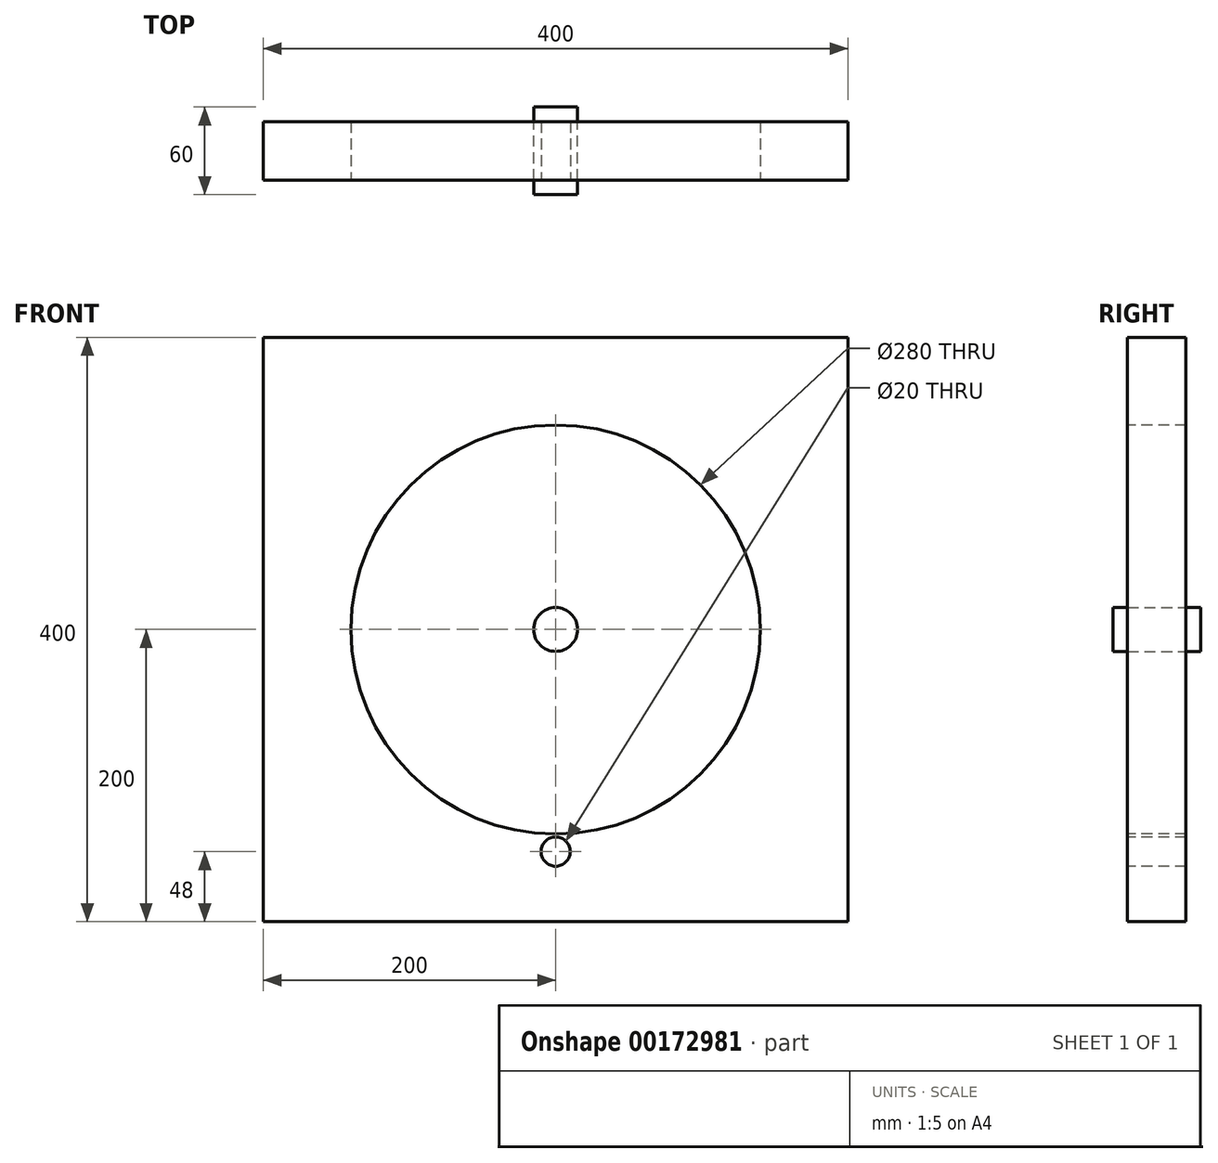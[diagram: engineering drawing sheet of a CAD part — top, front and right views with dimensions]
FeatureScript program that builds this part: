
annotation { "Feature Type Name" : "Feature", "Feature Type Description" : "" }
export const myFeature = defineFeature(function(context is Context, id is Id, definition is map)
    precondition{}
    {
        {
            var Q0;
            Q0=qCreatedBy(makeId("Top.planeOp"),FACE);
            var sketch = newSketch(context, id + "F0", { "sketchPlane" : qUnion([Q0])});
            skLineSegment(sketch, "E0.bottom", {"start": v(200, -20) * mm, "end": v(-200, -20) * mm});
            skLineSegment(sketch, "E0.top", {"start": v(200, 20) * mm, "end": v(-200, 20) * mm});
            skLineSegment(sketch, "E0.left", {"start": v(200, -20) * mm, "end": v(200, 20) * mm});
            skLineSegment(sketch, "E0.right", {"start": v(-200, -20) * mm, "end": v(-200, 20) * mm});
            skPoint(sketch, "E0.middle", {"position": v(0, 0) * mm});
            skSolve(sketch);
        }
        {
            var Q0;
            Q0 = qSketchRegion(id + "F0", true);
            extrude(context, id + "F1", {"entities" : qUnion([Q0]), "depth" : 200 * mm, "hasSecondDirection" : true, "secondDirectionOppositeDirection" : true, "secondDirectionDepth" : 200 * mm});
        }
        {
            var Q0;
            Q0=makeQuery(id+"F1.opExtrude","SWEPT_FACE",FACE,{"disambiguationData":[OSD([sQuery(id+"F0.wireOp",EDGE,"E0.bottom")])]});
            var sketch = newSketch(context, id + "F2", { "sketchPlane" : qUnion([Q0])});
            skCircle(sketch, "E1", {"center": v(0, 0) * mm, "radius": 140 * mm});
            skSolve(sketch);
        }
        {
            var Q0;
            Q0 = qSketchRegion(id + "F2", true);
            extrude(context, id + "F3", {"entities" : qUnion([Q0]), "operationType" : NewBodyOperationType.REMOVE, "oppositeDirection" : true, "depth" : 40 * mm});
        }
        {
            var Q0;
            Q0=qCreatedBy(makeId("Front.planeOp"),FACE);
            var sketch = newSketch(context, id + "F4", { "sketchPlane" : qUnion([Q0])});
            skCircle(sketch, "E2", {"center": v(0, 0) * mm, "radius": 15 * mm});
            skSolve(sketch);
        }
        {
            var Q0;
            Q0 = qSketchRegion(id + "F4", true);
            extrude(context, id + "F5", {"entities" : qUnion([Q0]), "depth" : 30 * mm, "hasSecondDirection" : true, "secondDirectionOppositeDirection" : true, "secondDirectionDepth" : 30 * mm});
        }
        {
            var Q0;
            Q0=makeQuery(id+"F1.opExtrude","SWEPT_FACE",FACE,{"disambiguationData":[OSD([sQuery(id+"F0.wireOp",EDGE,"E0.bottom")])]});
            var sketch = newSketch(context, id + "F6", { "sketchPlane" : qUnion([Q0])});
            skCircle(sketch, "E3", {"center": v(0, -152) * mm, "radius": 10 * mm});
            skSolve(sketch);
        }
        {
            var Q0;
            Q0 = qSketchRegion(id + "F6", true);
            extrude(context, id + "F7", {"entities" : qUnion([Q0]), "operationType" : NewBodyOperationType.REMOVE, "oppositeDirection" : true, "depth" : 40 * mm});
        }
    });
